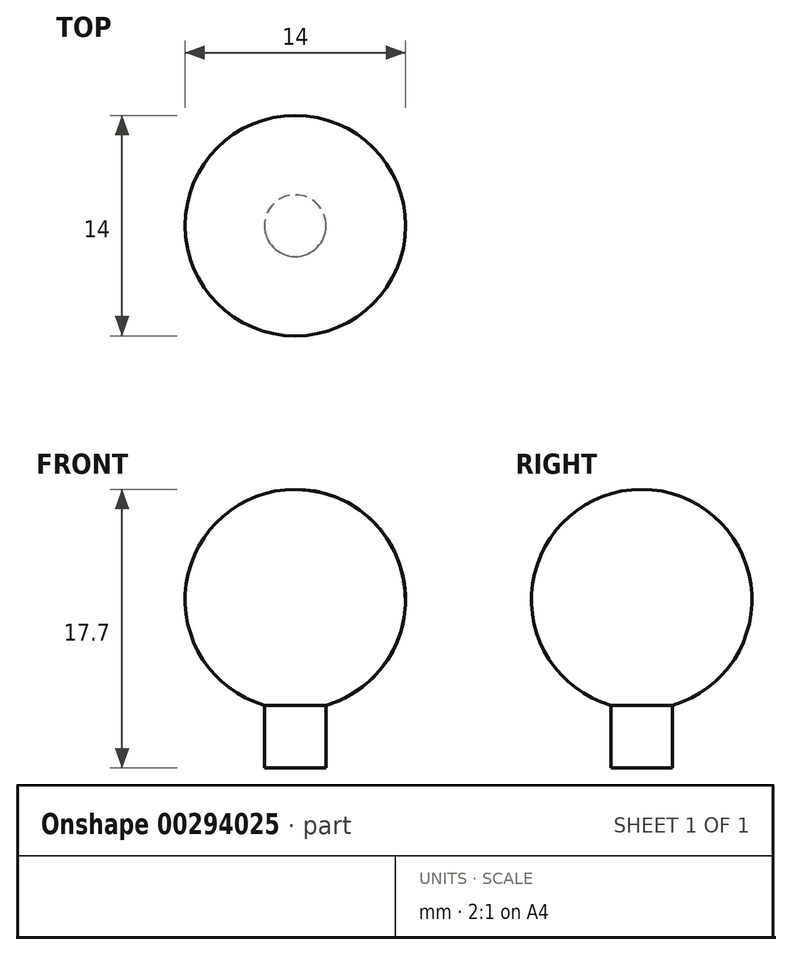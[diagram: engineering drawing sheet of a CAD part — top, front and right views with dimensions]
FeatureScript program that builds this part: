
annotation { "Feature Type Name" : "Feature", "Feature Type Description" : "" }
export const myFeature = defineFeature(function(context is Context, id is Id, definition is map)
    precondition{}
    {
        {
            var Q0;
            Q0=qCreatedBy(makeId("Front.planeOp"),FACE);
            var sketch = newSketch(context, id + "F0", { "sketchPlane" : qUnion([Q0])});
            skArc(sketch, "E0", {"start": v(0, 7) * mm, "mid": v(-6.93, 0.99) * mm, "end": v(-1.96, -6.72) * mm});
            skLineSegment(sketch, "E1.top", {"start": v(0, -10.7) * mm, "end": v(-1.96, -10.7) * mm});
            skLineSegment(sketch, "E1.right", {"start": v(-1.96, -6.72) * mm, "end": v(-1.96, -10.7) * mm});
            skPoint(sketch, "E1.middle", {"position": v(0, -7) * mm});
            skPoint(sketch, "E1.left.start.orphan", {"position": v(1.96, -3.3) * mm});
            skPoint(sketch, "E2.orphan", {"position": v(-1.96, -3.3) * mm});
            skLineSegment(sketch, "E3", {"start": v(0, -10.7) * mm, "end": v(0, 7) * mm});
            skPoint(sketch, "E4.orphan", {"position": v(1.96, -10.7) * mm});
            skLineSegment(sketch, "E5", {"start": v(0, -13.16) * mm, "end": v(0, 9.37) * mm, "construction": true});
            skSolve(sketch);
        }
        {
            var Q0;
            Q0=makeQuery(id+"F0.imprint","IMPRINT",FACE,{"disambiguationData":[TD([[makeQuery(id+"F0.imprint","IMPRINT",EDGE,{"derivedFrom":sQuery(id+"F0.wireOp",EDGE,"E0")}),1.0]])]});
            var Q1;
            Q1=sQuery(id+"F0.wireOp",EDGE,"E5");
            revolve(context, id + "F1", {"entities" : qUnion([Q0]), "axis" : qUnion([Q1]), "revolveType" : RevolveType.FULL});
        }
    });
